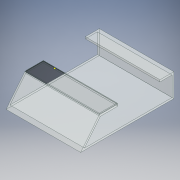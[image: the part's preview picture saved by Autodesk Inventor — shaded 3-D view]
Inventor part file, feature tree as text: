
AUTODESK INVENTOR PART (.ipt)
format: ipt  version: 2018 (Build 220112000, 112)  size: 147,968 bytes
history: native  units: in
note: dims shown in document units (in); Inventor stores cm internally (conversion verified against a paired STEP export)
features: sketch x4, extrude x2
ambient origin geometry x8: Origin, YZ Plane, XZ Plane, XY Plane, X Axis, Y Axis, Z Axis, Center Point
bodies: Solid1 (feature_tree)
feature tree (6):
  sketch  "Sketch1"  dims[d3=7.874in d4=1.5748in]
  extrude  "Extrusion1"  Depth=1.5748in
  extrude  "Extrusion2"  Depth=1.1811in
  sketch  "Sketch5"  dims[d9=0.3528in d10=0.1575in d12=0.1575in d14=0.1575in d15=0.1575in d16=0.1575in d17=0.1575in d18=0.1575in d19=6.2992in d20=0.0in d21=0.0394in d22=0.0394in d23=0.0394in d24=0.0394in d25=0.0787in d26=0.0in]
  sketch  "Sketch2"  dims[d5=1.9685in d6=1.1811in]
  sketch  "Sketch3"  dims[d7=1.5748in]
